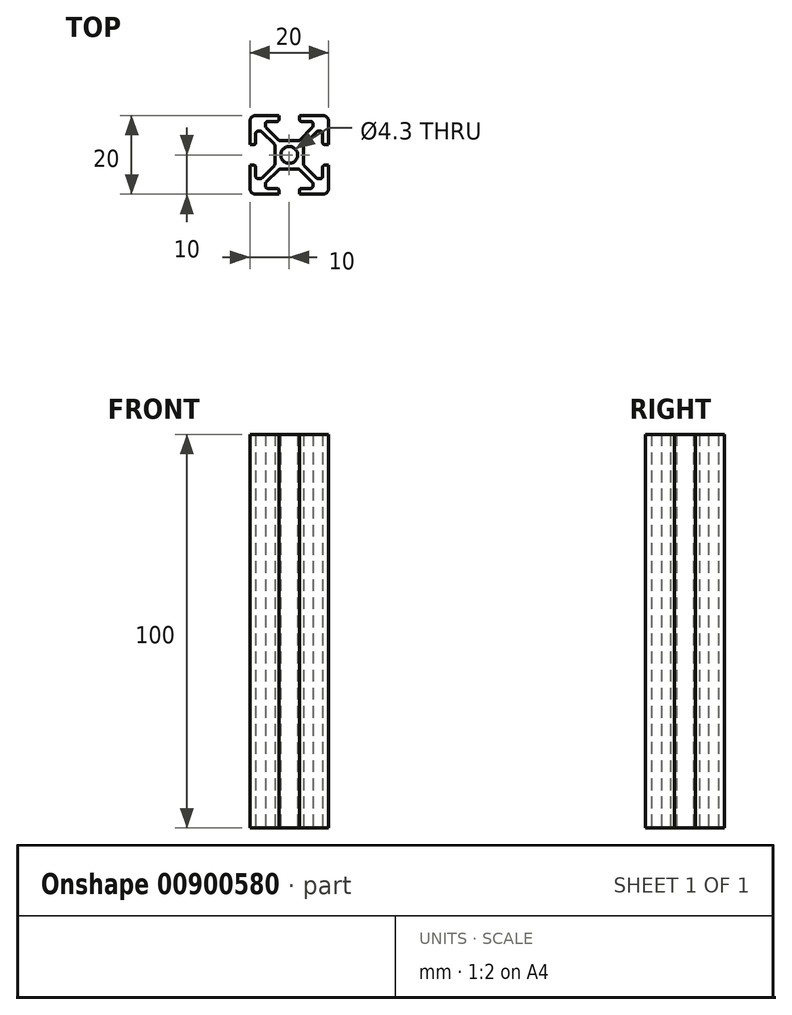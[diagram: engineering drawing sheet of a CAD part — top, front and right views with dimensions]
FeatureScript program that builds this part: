
annotation { "Feature Type Name" : "Feature", "Feature Type Description" : "" }
export const myFeature = defineFeature(function(context is Context, id is Id, definition is map)
    precondition{}
    {
        {
            var Q0;
            Q0=qCreatedBy(makeId("Top.planeOp"),FACE);
            var sketch = newSketch(context, id + "F0", { "sketchPlane" : qUnion([Q0])});
            skPoint(sketch, "E0.middle", {"position": v(0, 0) * mm});
            skCircle(sketch, "E1", {"center": v(0, 0) * mm, "radius": 2.15 * mm});
            skLineSegment(sketch, "E2.bottom", {"start": v(10, 10) * mm, "end": v(-10, 10) * mm});
            skLineSegment(sketch, "E2.top", {"start": v(10, -10) * mm, "end": v(-10, -10) * mm});
            skLineSegment(sketch, "E2.left", {"start": v(10, 10) * mm, "end": v(10, -10) * mm});
            skLineSegment(sketch, "E2.right", {"start": v(-10, 10) * mm, "end": v(-10, -10) * mm});
            skSolve(sketch);
        }
        {
            var Q0;
            Q0=makeQuery(id+"F0.imprint","IMPRINT",FACE,{"disambiguationData":[TD([[makeQuery(id+"F0.imprint","IMPRINT",EDGE,{"derivedFrom":sQuery(id+"F0.wireOp",EDGE,"E1")}),-1.0]])]});
            var sketch = newSketch(context, id + "F1", { "sketchPlane" : qUnion([Q0])});
            skLineSegment(sketch, "E3", {"start": v(-2.63, 10) * mm, "end": v(2.63, 10) * mm});
            skLineSegment(sketch, "E4", {"start": v(2.63, 10) * mm, "end": v(2.63, 8.5) * mm});
            skLineSegment(sketch, "E5", {"start": v(2.63, 8.5) * mm, "end": v(6, 8.5) * mm});
            skLineSegment(sketch, "E6", {"start": v(6, 8.5) * mm, "end": v(6, 7.06) * mm});
            skLineSegment(sketch, "E7", {"start": v(6, 7.06) * mm, "end": v(2.59, 3.65) * mm});
            skLineSegment(sketch, "E8", {"start": v(2.59, 3.65) * mm, "end": v(-2.59, 3.65) * mm});
            skLineSegment(sketch, "E9", {"start": v(-2.59, 3.65) * mm, "end": v(-6, 7.06) * mm});
            skLineSegment(sketch, "E10", {"start": v(-6, 7.06) * mm, "end": v(-6, 8.5) * mm});
            skLineSegment(sketch, "E11", {"start": v(-6, 8.5) * mm, "end": v(-2.63, 8.5) * mm});
            skLineSegment(sketch, "E12", {"start": v(-2.63, 8.5) * mm, "end": v(-2.63, 10) * mm});
            skPoint(sketch, "E13", {"position": v(0, 10) * mm});
            skPoint(sketch, "E14", {"position": v(0, 3.65) * mm});
            skPoint(sketch, "E15.center", {"position": v(0.01, -0.04) * mm});
            skLineSegment(sketch, "E16.0.0", {"start": v(-10, -10) * mm, "end": v(10, -10) * mm});
            skLineSegment(sketch, "E16.0.1", {"start": v(10, -10) * mm, "end": v(10, 10) * mm});
            skLineSegment(sketch, "E16.0.2", {"start": v(10, 10) * mm, "end": v(-10, 10) * mm});
            skLineSegment(sketch, "E16.0.3", {"start": v(-10, 10) * mm, "end": v(-10, -10) * mm});
            skLineSegment(sketch, "E17", {"start": v(0, 0) * mm, "end": v(10, 10) * mm, "construction": true});
            skLineSegment(sketch, "E18.1.0", {"start": v(-8.5, -2.63) * mm, "end": v(-10, -2.63) * mm});
            skLineSegment(sketch, "E18.1.1", {"start": v(-8.5, -6) * mm, "end": v(-8.5, -2.63) * mm});
            skLineSegment(sketch, "E18.1.2", {"start": v(-7.06, -6) * mm, "end": v(-8.5, -6) * mm});
            skLineSegment(sketch, "E18.1.3", {"start": v(-3.65, -2.59) * mm, "end": v(-7.06, -6) * mm});
            skLineSegment(sketch, "E18.1.4", {"start": v(-3.65, 2.59) * mm, "end": v(-3.65, -2.59) * mm});
            skLineSegment(sketch, "E18.1.5", {"start": v(-7.06, 6) * mm, "end": v(-3.65, 2.59) * mm});
            skLineSegment(sketch, "E18.1.6", {"start": v(-8.5, 6) * mm, "end": v(-7.06, 6) * mm});
            skLineSegment(sketch, "E18.1.7", {"start": v(-8.5, 2.63) * mm, "end": v(-8.5, 6) * mm});
            skLineSegment(sketch, "E18.1.8", {"start": v(-10, 2.63) * mm, "end": v(-8.5, 2.63) * mm});
            skLineSegment(sketch, "E18.2.0", {"start": v(2.63, -8.5) * mm, "end": v(2.63, -10) * mm});
            skLineSegment(sketch, "E18.2.1", {"start": v(6, -8.5) * mm, "end": v(2.63, -8.5) * mm});
            skLineSegment(sketch, "E18.2.2", {"start": v(6, -7.06) * mm, "end": v(6, -8.5) * mm});
            skLineSegment(sketch, "E18.2.3", {"start": v(2.59, -3.65) * mm, "end": v(6, -7.06) * mm});
            skLineSegment(sketch, "E18.2.4", {"start": v(-2.59, -3.65) * mm, "end": v(2.59, -3.65) * mm});
            skLineSegment(sketch, "E18.2.5", {"start": v(-6, -7.06) * mm, "end": v(-2.59, -3.65) * mm});
            skLineSegment(sketch, "E18.2.6", {"start": v(-6, -8.5) * mm, "end": v(-6, -7.06) * mm});
            skLineSegment(sketch, "E18.2.7", {"start": v(-2.63, -8.5) * mm, "end": v(-6, -8.5) * mm});
            skLineSegment(sketch, "E18.2.8", {"start": v(-2.63, -10) * mm, "end": v(-2.63, -8.5) * mm});
            skLineSegment(sketch, "E18.3.0", {"start": v(8.5, 2.63) * mm, "end": v(10, 2.63) * mm});
            skLineSegment(sketch, "E18.3.1", {"start": v(8.5, 6) * mm, "end": v(8.5, 2.63) * mm});
            skLineSegment(sketch, "E18.3.2", {"start": v(7.06, 6) * mm, "end": v(8.5, 6) * mm});
            skLineSegment(sketch, "E18.3.3", {"start": v(3.65, 2.59) * mm, "end": v(7.06, 6) * mm});
            skLineSegment(sketch, "E18.3.4", {"start": v(3.65, -2.59) * mm, "end": v(3.65, 2.59) * mm});
            skLineSegment(sketch, "E18.3.5", {"start": v(7.06, -6) * mm, "end": v(3.65, -2.59) * mm});
            skLineSegment(sketch, "E18.3.6", {"start": v(8.5, -6) * mm, "end": v(7.06, -6) * mm});
            skLineSegment(sketch, "E18.3.7", {"start": v(8.5, -2.63) * mm, "end": v(8.5, -6) * mm});
            skLineSegment(sketch, "E18.3.8", {"start": v(10, -2.63) * mm, "end": v(8.5, -2.63) * mm});
            skPoint(sketch, "E18.center", {"position": v(0, 0) * mm});
            skSolve(sketch);
        }
        {
            var Q0;
            Q0=makeQuery(id+"F0.imprint","IMPRINT",FACE,{"disambiguationData":[TD([[makeQuery(id+"F0.imprint","IMPRINT",EDGE,{"derivedFrom":sQuery(id+"F0.wireOp",EDGE,"E1")}),-1.0]])]});
            extrude(context, id + "F2", {"entities" : qUnion([Q0]), "flatOperationType" : FlatOperationType.REMOVE, "thickness1" : 5 * mm, "thickness2" : 0 * mm, "depth" : 100 * mm, "offsetDistance" : 25 * mm, "startOffsetBound" : StartOffsetType.BLIND, "startOffsetDistance" : 25 * mm, "domain" : OperationDomain.MODEL});
        }
        {
            var Q0;
            {var subQ0=sQuery(id+"F1.wireOp",EDGE,"E18.1.0");Q0=makeQuery(id+"F1.imprint","IMPRINT",FACE,{"disambiguationData":[TD([[makeQuery(id+"F1.imprint","IMPRINT",EDGE,{"derivedFrom":subQ0}),-1.0]])]});}
            var Q1;
            {var subQ0=sQuery(id+"F1.wireOp",EDGE,"E18.2.0");Q1=makeQuery(id+"F1.imprint","IMPRINT",FACE,{"disambiguationData":[TD([[makeQuery(id+"F1.imprint","IMPRINT",EDGE,{"derivedFrom":subQ0}),-1.0]])]});}
            var Q2;
            {var subQ0=sQuery(id+"F1.wireOp",EDGE,"E18.3.0");Q2=makeQuery(id+"F1.imprint","IMPRINT",FACE,{"disambiguationData":[TD([[makeQuery(id+"F1.imprint","IMPRINT",EDGE,{"derivedFrom":subQ0}),-1.0]])]});}
            var Q3;
            {var subQ0=sQuery(id+"F1.wireOp",EDGE,"E4");Q3=makeQuery(id+"F1.imprint","IMPRINT",FACE,{"disambiguationData":[TD([[makeQuery(id+"F1.imprint","IMPRINT",EDGE,{"derivedFrom":subQ0}),-1.0]])]});}
            extrude(context, id + "F3", {"entities" : qUnion([Q0, Q1, Q2, Q3]), "operationType" : NewBodyOperationType.REMOVE, "endBound" : BoundingType.THROUGH_ALL, "depth" : 25 * mm, "offsetDistance" : 25 * mm});
        }
        {
            var Q0;
            Q0=makeQuery(id+"F2.opExtrude","SWEPT_EDGE",EDGE,{"disambiguationData":[OSD([sQuery(id+"F0.wireOp",EDGE,"E2.top"),sQuery(id+"F0.wireOp",EDGE,"E2.left")])]});
            var Q1;
            Q1=makeQuery(id+"F2.opExtrude","SWEPT_EDGE",EDGE,{"disambiguationData":[OSD([sQuery(id+"F0.wireOp",EDGE,"E2.top"),sQuery(id+"F0.wireOp",EDGE,"E2.right")])]});
            var Q2;
            Q2=makeQuery(id+"F2.opExtrude","SWEPT_EDGE",EDGE,{"disambiguationData":[OSD([sQuery(id+"F0.wireOp",EDGE,"E2.bottom"),sQuery(id+"F0.wireOp",EDGE,"E2.left")])]});
            var Q3;
            Q3=makeQuery(id+"F2.opExtrude","SWEPT_EDGE",EDGE,{"disambiguationData":[OSD([sQuery(id+"F0.wireOp",EDGE,"E2.bottom"),sQuery(id+"F0.wireOp",EDGE,"E2.right")])]});
            fillet(context, id + "F4", {"entities" : qUnion([Q0, Q1, Q2, Q3]), "radius" : 1.5 * mm, "tangentPropagation" : true, "allowEdgeOverflow" : false});
        }
        {
            var Q0;
            Q0=makeQuery(id+"F3.boolean.opBoolean","COPY",EDGE,{"derivedFrom":makeQuery(id+"F3.opExtrude","SWEPT_EDGE",EDGE,{"disambiguationData":[OSD([sQuery(id+"F1.wireOp",EDGE,"E16.0.0"),sQuery(id+"F1.wireOp",EDGE,"E18.2.8")])]})});
            var Q1;
            Q1=makeQuery(id+"F3.boolean.opBoolean","COPY",EDGE,{"derivedFrom":makeQuery(id+"F3.opExtrude","SWEPT_EDGE",EDGE,{"disambiguationData":[OSD([sQuery(id+"F1.wireOp",EDGE,"E16.0.3"),sQuery(id+"F1.wireOp",EDGE,"E18.1.8")])]})});
            var Q2;
            Q2=makeQuery(id+"F3.boolean.opBoolean","COPY",EDGE,{"derivedFrom":makeQuery(id+"F3.opExtrude","SWEPT_EDGE",EDGE,{"disambiguationData":[OSD([sQuery(id+"F1.wireOp",EDGE,"E12"),sQuery(id+"F1.wireOp",EDGE,"E16.0.2")])]})});
            var Q3;
            Q3=makeQuery(id+"F3.boolean.opBoolean","COPY",EDGE,{"derivedFrom":makeQuery(id+"F3.opExtrude","SWEPT_EDGE",EDGE,{"disambiguationData":[OSD([sQuery(id+"F1.wireOp",EDGE,"E16.0.0"),sQuery(id+"F1.wireOp",EDGE,"E18.2.0")])]})});
            var Q4;
            Q4=makeQuery(id+"F3.boolean.opBoolean","COPY",EDGE,{"derivedFrom":makeQuery(id+"F3.opExtrude","SWEPT_EDGE",EDGE,{"disambiguationData":[OSD([sQuery(id+"F1.wireOp",EDGE,"E16.0.1"),sQuery(id+"F1.wireOp",EDGE,"E18.3.0")])]})});
            var Q5;
            Q5=makeQuery(id+"F3.boolean.opBoolean","COPY",EDGE,{"derivedFrom":makeQuery(id+"F3.opExtrude","SWEPT_EDGE",EDGE,{"disambiguationData":[OSD([sQuery(id+"F1.wireOp",EDGE,"E16.0.1"),sQuery(id+"F1.wireOp",EDGE,"E18.3.8")])]})});
            var Q6;
            Q6=makeQuery(id+"F3.boolean.opBoolean","COPY",EDGE,{"derivedFrom":makeQuery(id+"F3.opExtrude","SWEPT_EDGE",EDGE,{"disambiguationData":[OSD([sQuery(id+"F1.wireOp",EDGE,"E16.0.3"),sQuery(id+"F1.wireOp",EDGE,"E18.1.0")])]})});
            var Q7;
            Q7=makeQuery(id+"F3.boolean.opBoolean","COPY",EDGE,{"derivedFrom":makeQuery(id+"F3.opExtrude","SWEPT_EDGE",EDGE,{"disambiguationData":[OSD([sQuery(id+"F1.wireOp",EDGE,"E4"),sQuery(id+"F1.wireOp",EDGE,"E16.0.2")])]})});
            var Q8;
            Q8=makeQuery(id+"F3.boolean.opBoolean","COPY",EDGE,{"derivedFrom":makeQuery(id+"F3.opExtrude","SWEPT_EDGE",EDGE,{"disambiguationData":[OSD([sQuery(id+"F1.wireOp",EDGE,"E18.2.6"),sQuery(id+"F1.wireOp",EDGE,"E18.2.7")])]})});
            var Q9;
            Q9=makeQuery(id+"F3.boolean.opBoolean","COPY",EDGE,{"derivedFrom":makeQuery(id+"F3.opExtrude","SWEPT_EDGE",EDGE,{"disambiguationData":[OSD([sQuery(id+"F1.wireOp",EDGE,"E18.2.7"),sQuery(id+"F1.wireOp",EDGE,"E18.2.8")])]})});
            var Q10;
            Q10=makeQuery(id+"F3.boolean.opBoolean","COPY",EDGE,{"derivedFrom":makeQuery(id+"F3.opExtrude","SWEPT_EDGE",EDGE,{"disambiguationData":[OSD([sQuery(id+"F1.wireOp",EDGE,"E18.2.0"),sQuery(id+"F1.wireOp",EDGE,"E18.2.1")])]})});
            var Q11;
            Q11=makeQuery(id+"F3.boolean.opBoolean","COPY",EDGE,{"derivedFrom":makeQuery(id+"F3.opExtrude","SWEPT_EDGE",EDGE,{"disambiguationData":[OSD([sQuery(id+"F1.wireOp",EDGE,"E18.1.7"),sQuery(id+"F1.wireOp",EDGE,"E18.1.8")])]})});
            var Q12;
            Q12=makeQuery(id+"F3.boolean.opBoolean","COPY",EDGE,{"derivedFrom":makeQuery(id+"F3.opExtrude","SWEPT_EDGE",EDGE,{"disambiguationData":[OSD([sQuery(id+"F1.wireOp",EDGE,"E18.1.0"),sQuery(id+"F1.wireOp",EDGE,"E18.1.1")])]})});
            var Q13;
            Q13=makeQuery(id+"F3.boolean.opBoolean","COPY",EDGE,{"derivedFrom":makeQuery(id+"F3.opExtrude","SWEPT_EDGE",EDGE,{"disambiguationData":[OSD([sQuery(id+"F1.wireOp",EDGE,"E18.3.7"),sQuery(id+"F1.wireOp",EDGE,"E18.3.8")])]})});
            var Q14;
            Q14=makeQuery(id+"F3.boolean.opBoolean","COPY",EDGE,{"derivedFrom":makeQuery(id+"F3.opExtrude","SWEPT_EDGE",EDGE,{"disambiguationData":[OSD([sQuery(id+"F1.wireOp",EDGE,"E18.3.0"),sQuery(id+"F1.wireOp",EDGE,"E18.3.1")])]})});
            var Q15;
            Q15=makeQuery(id+"F3.boolean.opBoolean","COPY",EDGE,{"derivedFrom":makeQuery(id+"F3.opExtrude","SWEPT_EDGE",EDGE,{"disambiguationData":[OSD([sQuery(id+"F1.wireOp",EDGE,"E4"),sQuery(id+"F1.wireOp",EDGE,"E5")])]})});
            var Q16;
            Q16=makeQuery(id+"F3.boolean.opBoolean","COPY",EDGE,{"derivedFrom":makeQuery(id+"F3.opExtrude","SWEPT_EDGE",EDGE,{"disambiguationData":[OSD([sQuery(id+"F1.wireOp",EDGE,"E5"),sQuery(id+"F1.wireOp",EDGE,"E6")])]})});
            var Q17;
            Q17=makeQuery(id+"F3.boolean.opBoolean","COPY",EDGE,{"derivedFrom":makeQuery(id+"F3.opExtrude","SWEPT_EDGE",EDGE,{"disambiguationData":[OSD([sQuery(id+"F1.wireOp",EDGE,"E18.3.1"),sQuery(id+"F1.wireOp",EDGE,"E18.3.2")])]})});
            var Q18;
            Q18=makeQuery(id+"F3.boolean.opBoolean","COPY",EDGE,{"derivedFrom":makeQuery(id+"F3.opExtrude","SWEPT_EDGE",EDGE,{"disambiguationData":[OSD([sQuery(id+"F1.wireOp",EDGE,"E18.3.2"),sQuery(id+"F1.wireOp",EDGE,"E18.3.3")])]})});
            var Q19;
            Q19=makeQuery(id+"F3.boolean.opBoolean","COPY",EDGE,{"derivedFrom":makeQuery(id+"F3.opExtrude","SWEPT_EDGE",EDGE,{"disambiguationData":[OSD([sQuery(id+"F1.wireOp",EDGE,"E6"),sQuery(id+"F1.wireOp",EDGE,"E7")])]})});
            var Q20;
            Q20=makeQuery(id+"F3.boolean.opBoolean","COPY",EDGE,{"derivedFrom":makeQuery(id+"F3.opExtrude","SWEPT_EDGE",EDGE,{"disambiguationData":[OSD([sQuery(id+"F1.wireOp",EDGE,"E18.2.4"),sQuery(id+"F1.wireOp",EDGE,"E18.2.5")])]})});
            var Q21;
            Q21=makeQuery(id+"F3.boolean.opBoolean","COPY",EDGE,{"derivedFrom":makeQuery(id+"F3.opExtrude","SWEPT_EDGE",EDGE,{"disambiguationData":[OSD([sQuery(id+"F1.wireOp",EDGE,"E18.2.3"),sQuery(id+"F1.wireOp",EDGE,"E18.2.4")])]})});
            var Q22;
            Q22=makeQuery(id+"F3.boolean.opBoolean","COPY",EDGE,{"derivedFrom":makeQuery(id+"F3.opExtrude","SWEPT_EDGE",EDGE,{"disambiguationData":[OSD([sQuery(id+"F1.wireOp",EDGE,"E18.3.3"),sQuery(id+"F1.wireOp",EDGE,"E18.3.4")])]})});
            var Q23;
            Q23=makeQuery(id+"F3.boolean.opBoolean","COPY",EDGE,{"derivedFrom":makeQuery(id+"F3.opExtrude","SWEPT_EDGE",EDGE,{"disambiguationData":[OSD([sQuery(id+"F1.wireOp",EDGE,"E18.3.4"),sQuery(id+"F1.wireOp",EDGE,"E18.3.5")])]})});
            var Q24;
            Q24=makeQuery(id+"F3.boolean.opBoolean","COPY",EDGE,{"derivedFrom":makeQuery(id+"F3.opExtrude","SWEPT_EDGE",EDGE,{"disambiguationData":[OSD([sQuery(id+"F1.wireOp",EDGE,"E18.1.3"),sQuery(id+"F1.wireOp",EDGE,"E18.1.4")])]})});
            var Q25;
            Q25=makeQuery(id+"F3.boolean.opBoolean","COPY",EDGE,{"derivedFrom":makeQuery(id+"F3.opExtrude","SWEPT_EDGE",EDGE,{"disambiguationData":[OSD([sQuery(id+"F1.wireOp",EDGE,"E18.1.4"),sQuery(id+"F1.wireOp",EDGE,"E18.1.5")])]})});
            var Q26;
            Q26=makeQuery(id+"F3.boolean.opBoolean","COPY",EDGE,{"derivedFrom":makeQuery(id+"F3.opExtrude","SWEPT_EDGE",EDGE,{"disambiguationData":[OSD([sQuery(id+"F1.wireOp",EDGE,"E7"),sQuery(id+"F1.wireOp",EDGE,"E8")])]})});
            var Q27;
            Q27=makeQuery(id+"F3.boolean.opBoolean","COPY",EDGE,{"derivedFrom":makeQuery(id+"F3.opExtrude","SWEPT_EDGE",EDGE,{"disambiguationData":[OSD([sQuery(id+"F1.wireOp",EDGE,"E8"),sQuery(id+"F1.wireOp",EDGE,"E9")])]})});
            var Q28;
            Q28=makeQuery(id+"F3.boolean.opBoolean","COPY",EDGE,{"derivedFrom":makeQuery(id+"F3.opExtrude","SWEPT_EDGE",EDGE,{"disambiguationData":[OSD([sQuery(id+"F1.wireOp",EDGE,"E10"),sQuery(id+"F1.wireOp",EDGE,"E11")])]})});
            var Q29;
            Q29=makeQuery(id+"F3.boolean.opBoolean","COPY",EDGE,{"derivedFrom":makeQuery(id+"F3.opExtrude","SWEPT_EDGE",EDGE,{"disambiguationData":[OSD([sQuery(id+"F1.wireOp",EDGE,"E9"),sQuery(id+"F1.wireOp",EDGE,"E10")])]})});
            var Q30;
            Q30=makeQuery(id+"F3.boolean.opBoolean","COPY",EDGE,{"derivedFrom":makeQuery(id+"F3.opExtrude","SWEPT_EDGE",EDGE,{"disambiguationData":[OSD([sQuery(id+"F1.wireOp",EDGE,"E11"),sQuery(id+"F1.wireOp",EDGE,"E12")])]})});
            var Q31;
            Q31=makeQuery(id+"F3.boolean.opBoolean","COPY",EDGE,{"derivedFrom":makeQuery(id+"F3.opExtrude","SWEPT_EDGE",EDGE,{"disambiguationData":[OSD([sQuery(id+"F1.wireOp",EDGE,"E18.3.6"),sQuery(id+"F1.wireOp",EDGE,"E18.3.7")])]})});
            var Q32;
            Q32=makeQuery(id+"F3.boolean.opBoolean","COPY",EDGE,{"derivedFrom":makeQuery(id+"F3.opExtrude","SWEPT_EDGE",EDGE,{"disambiguationData":[OSD([sQuery(id+"F1.wireOp",EDGE,"E18.3.5"),sQuery(id+"F1.wireOp",EDGE,"E18.3.6")])]})});
            var Q33;
            Q33=makeQuery(id+"F3.boolean.opBoolean","COPY",EDGE,{"derivedFrom":makeQuery(id+"F3.opExtrude","SWEPT_EDGE",EDGE,{"disambiguationData":[OSD([sQuery(id+"F1.wireOp",EDGE,"E18.1.1"),sQuery(id+"F1.wireOp",EDGE,"E18.1.2")])]})});
            var Q34;
            Q34=makeQuery(id+"F3.boolean.opBoolean","COPY",EDGE,{"derivedFrom":makeQuery(id+"F3.opExtrude","SWEPT_EDGE",EDGE,{"disambiguationData":[OSD([sQuery(id+"F1.wireOp",EDGE,"E18.1.2"),sQuery(id+"F1.wireOp",EDGE,"E18.1.3")])]})});
            var Q35;
            Q35=makeQuery(id+"F3.boolean.opBoolean","COPY",EDGE,{"derivedFrom":makeQuery(id+"F3.opExtrude","SWEPT_EDGE",EDGE,{"disambiguationData":[OSD([sQuery(id+"F1.wireOp",EDGE,"E18.2.5"),sQuery(id+"F1.wireOp",EDGE,"E18.2.6")])]})});
            var Q36;
            Q36=makeQuery(id+"F3.boolean.opBoolean","COPY",EDGE,{"derivedFrom":makeQuery(id+"F3.opExtrude","SWEPT_EDGE",EDGE,{"disambiguationData":[OSD([sQuery(id+"F1.wireOp",EDGE,"E18.2.2"),sQuery(id+"F1.wireOp",EDGE,"E18.2.3")])]})});
            var Q37;
            Q37=makeQuery(id+"F3.boolean.opBoolean","COPY",EDGE,{"derivedFrom":makeQuery(id+"F3.opExtrude","SWEPT_EDGE",EDGE,{"disambiguationData":[OSD([sQuery(id+"F1.wireOp",EDGE,"E18.2.1"),sQuery(id+"F1.wireOp",EDGE,"E18.2.2")])]})});
            var Q38;
            Q38=makeQuery(id+"F3.boolean.opBoolean","COPY",EDGE,{"derivedFrom":makeQuery(id+"F3.opExtrude","SWEPT_EDGE",EDGE,{"disambiguationData":[OSD([sQuery(id+"F1.wireOp",EDGE,"E18.1.6"),sQuery(id+"F1.wireOp",EDGE,"E18.1.7")])]})});
            var Q39;
            Q39=makeQuery(id+"F3.boolean.opBoolean","COPY",EDGE,{"derivedFrom":makeQuery(id+"F3.opExtrude","SWEPT_EDGE",EDGE,{"disambiguationData":[OSD([sQuery(id+"F1.wireOp",EDGE,"E18.1.5"),sQuery(id+"F1.wireOp",EDGE,"E18.1.6")])]})});
            fillet(context, id + "F5", {"entities" : qUnion([Q0, Q1, Q2, Q3, Q4, Q5, Q6, Q7, Q8, Q9, Q10, Q11, Q12, Q13, Q14, Q15, Q16, Q17, Q18, Q19, Q20, Q21, Q22, Q23, Q24, Q25, Q26, Q27, Q28, Q29, Q30, Q31, Q32, Q33, Q34, Q35, Q36, Q37, Q38, Q39]), "radius" : 0.5 * mm, "tangentPropagation" : true, "allowEdgeOverflow" : false});
        }
    });
